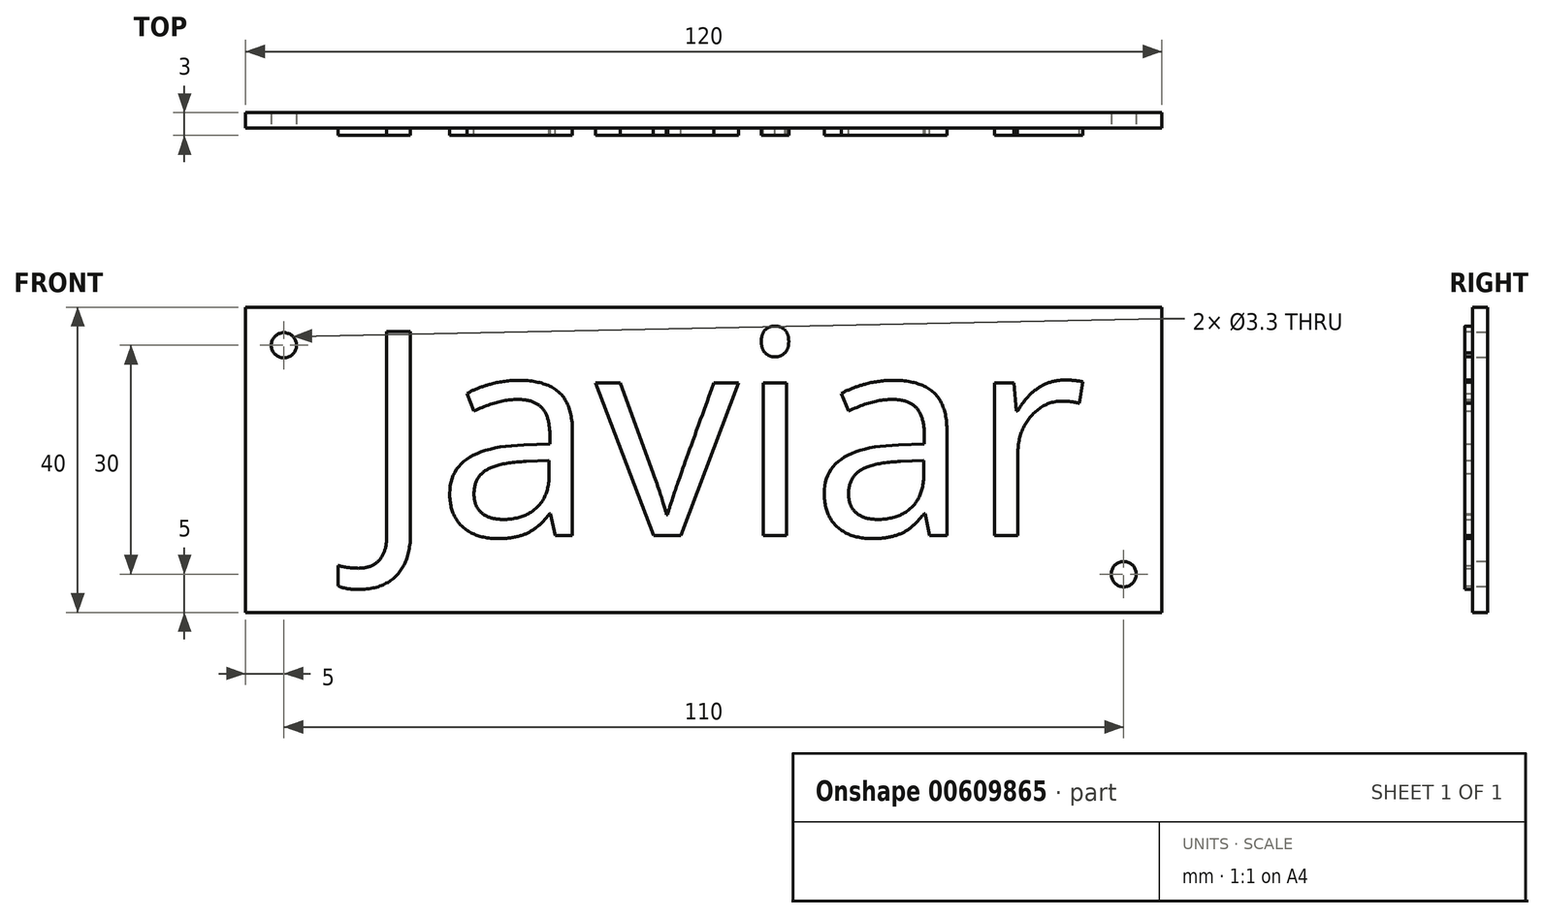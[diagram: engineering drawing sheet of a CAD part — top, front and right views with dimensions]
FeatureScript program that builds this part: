
annotation { "Feature Type Name" : "Feature", "Feature Type Description" : "" }
export const myFeature = defineFeature(function(context is Context, id is Id, definition is map)
    precondition{}
    {
        {
            var Q0;
            Q0=qCreatedBy(makeId("Front.planeOp"),FACE);
            var sketch = newSketch(context, id + "F0", { "sketchPlane" : qUnion([Q0])});
            skLineSegment(sketch, "E0.bottom", {"start": v(60, -20) * mm, "end": v(-60, -20) * mm});
            skLineSegment(sketch, "E0.top", {"start": v(60, 20) * mm, "end": v(-60, 20) * mm});
            skLineSegment(sketch, "E0.left", {"start": v(60, -20) * mm, "end": v(60, 20) * mm});
            skLineSegment(sketch, "E0.right", {"start": v(-60, -20) * mm, "end": v(-60, 20) * mm});
            skPoint(sketch, "E0.middle", {"position": v(0, 0) * mm});
            skSolve(sketch);
        }
        {
            var Q0;
            Q0=makeQuery(id+"F0.imprint","IMPRINT",FACE,{"disambiguationData":[TD([[makeQuery(id+"F0.imprint","IMPRINT",EDGE,{"derivedFrom":sQuery(id+"F0.wireOp",EDGE,"E0.bottom")}),-1.0]])]});
            extrude(context, id + "F1", {"entities" : qUnion([Q0]), "depth" : 2 * mm});
        }
        {
            var Q0;
            Q0=makeQuery(id+"F1.opExtrude","CAP_FACE",FACE,{"disambiguationData":[OSD([sQuery(id+"F0.wireOp",EDGE,"E0.bottom"),sQuery(id+"F0.wireOp",EDGE,"E0.top"),sQuery(id+"F0.wireOp",EDGE,"E0.left"),sQuery(id+"F0.wireOp",EDGE,"E0.right")])],"isStart":false});
            var sketch = newSketch(context, id + "F2", { "sketchPlane" : qUnion([Q0])});
            skPoint(sketch, "E1", {"position": v(-55, 15) * mm});
            skPoint(sketch, "E2", {"position": v(55, -15) * mm});
            skSolve(sketch);
        }
        {
            var Q0;
            Q0=sQuery(id+"F2.wireOp",VERTEX,"E1");
            var Q1;
            Q1=sQuery(id+"F2.wireOp",VERTEX,"E2");
            var Q2;
            Q2=makeQuery(id+"F1.opExtrude","SWEPT_BODY",BODY,{"disambiguationData":[OSD([sQuery(id+"F0.wireOp",EDGE,"E0.bottom"),sQuery(id+"F0.wireOp",EDGE,"E0.top"),sQuery(id+"F0.wireOp",EDGE,"E0.left"),sQuery(id+"F0.wireOp",EDGE,"E0.right")])]});
            hole(context, id + "F3", {"style" : HoleStyle.SIMPLE, "endStyle" : HoleEndStyle.THROUGH, "holeDiameter" : 3.3 * mm, "locations" : qUnion([Q0, Q1]), "scope" : qUnion([Q2]), "isTappedThrough" : true});
        }
        {
            var Q0;
            Q0=makeQuery(id+"F1.opExtrude","CAP_FACE",FACE,{"disambiguationData":[OSD([sQuery(id+"F0.wireOp",EDGE,"E0.bottom"),sQuery(id+"F0.wireOp",EDGE,"E0.top"),sQuery(id+"F0.wireOp",EDGE,"E0.left"),sQuery(id+"F0.wireOp",EDGE,"E0.right")])],"isStart":false});
            var sketch = newSketch(context, id + "F4", { "sketchPlane" : qUnion([Q0])});
            skText(sketch, "E3", { "text": "Javiar", "fontName": "OpenSans-Regular.ttf"});
            const initialGuessF4  = {"E3": [-0.045, -0.00996, 1, 0, 0.02696]};
            skSetInitialGuess(sketch, initialGuessF4);
            skSolve(sketch);
        }
        {
            var Q0;
            Q0 = qSketchRegion(id + "F4", true);
            extrude(context, id + "F5", {"entities" : qUnion([Q0]), "operationType" : NewBodyOperationType.ADD, "depth" : 1 * mm, "offsetDistance" : 25 * mm});
        }
    });
